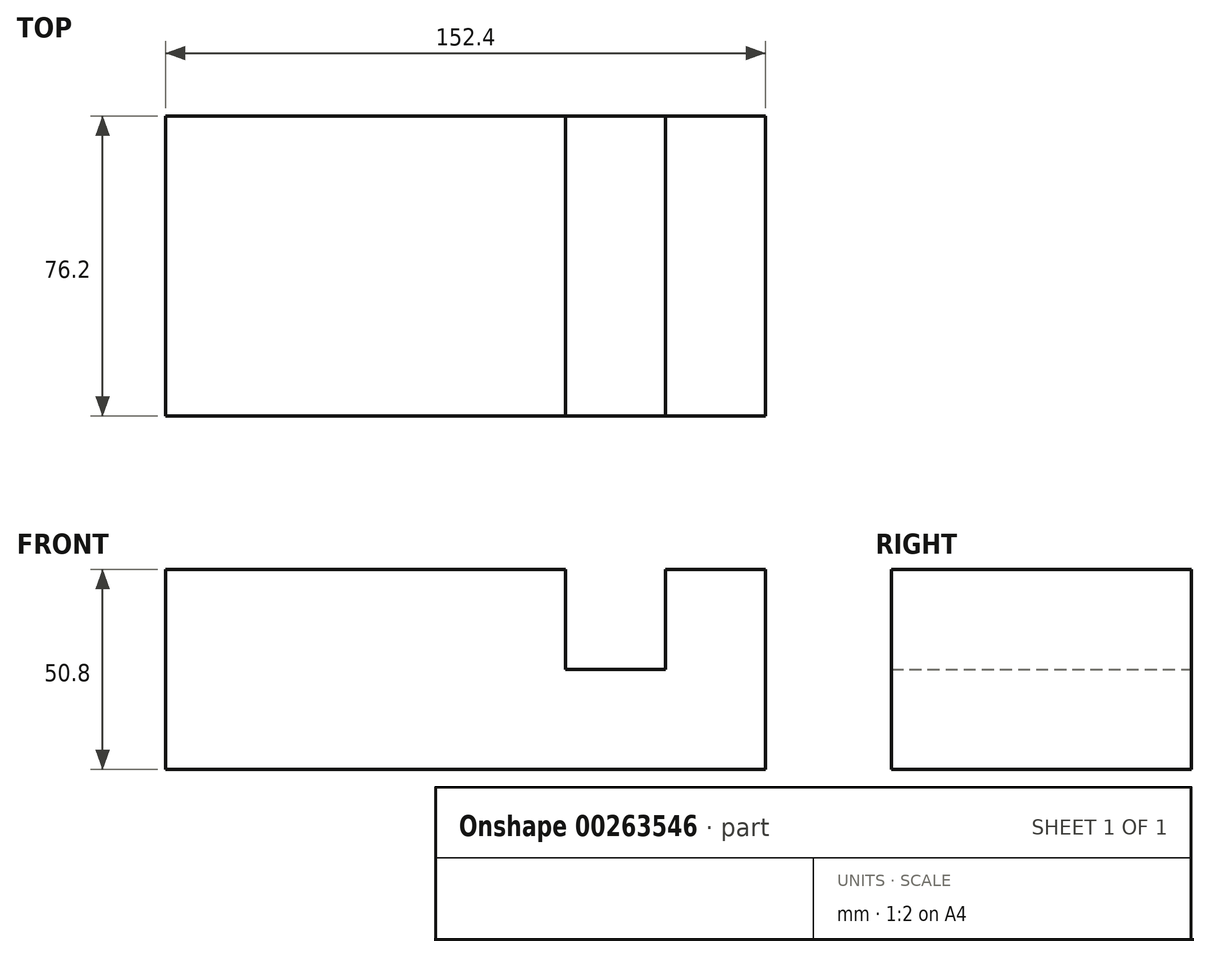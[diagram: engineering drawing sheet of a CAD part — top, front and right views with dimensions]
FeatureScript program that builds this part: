
annotation { "Feature Type Name" : "Feature", "Feature Type Description" : "" }
export const myFeature = defineFeature(function(context is Context, id is Id, definition is map)
    precondition{}
    {
        {
            var Q0;
            Q0=qCreatedBy(makeId("Front.planeOp"),FACE);
            var sketch = newSketch(context, id + "F0", { "sketchPlane" : qUnion([Q0])});
            skLineSegment(sketch, "E0", {"start": v(-77.7, -25.4) * mm, "end": v(74.7, -25.4) * mm});
            skLineSegment(sketch, "E1", {"start": v(-77.7, -25.4) * mm, "end": v(-77.7, 25.4) * mm});
            skLineSegment(sketch, "E2", {"start": v(-77.7, 25.4) * mm, "end": v(23.9, 25.4) * mm});
            skLineSegment(sketch, "E3", {"start": v(23.9, 25.4) * mm, "end": v(23.9, 0) * mm});
            skLineSegment(sketch, "E4", {"start": v(23.9, 0) * mm, "end": v(49.3, 0) * mm});
            skLineSegment(sketch, "E5", {"start": v(49.3, 0) * mm, "end": v(49.3, 25.4) * mm});
            skLineSegment(sketch, "E6", {"start": v(49.3, 25.4) * mm, "end": v(74.7, 25.4) * mm});
            skLineSegment(sketch, "E7", {"start": v(74.7, 25.4) * mm, "end": v(74.7, -25.4) * mm});
            skSolve(sketch);
        }
        {
            var Q0;
            Q0=makeQuery(id+"F0.imprint","IMPRINT",FACE,{"disambiguationData":[TD([[makeQuery(id+"F0.imprint","IMPRINT",EDGE,{"derivedFrom":sQuery(id+"F0.wireOp",EDGE,"E0")}),1.0]])]});
            extrude(context, id + "F1", {"entities" : qUnion([Q0]), "depth" : 76.2 * mm});
        }
    });
